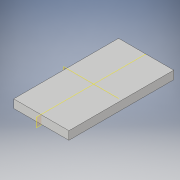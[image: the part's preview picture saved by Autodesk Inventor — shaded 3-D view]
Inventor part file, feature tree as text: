
AUTODESK INVENTOR PART (.ipt)
format: ipt  version: 2017 (Build 210142000, 142)  size: 172,032 bytes
history: native  units: in
note: dims shown in document units (in); Inventor stores cm internally (conversion verified against a paired STEP export)
features: extrude x4, sketch x4, plane x2, mirror x2, projected_geometry x1
ambient origin geometry x8: Origin, YZ Plane, XZ Plane, XY Plane, X Axis, Y Axis, Z Axis, Center Point
bodies: Solid1 (feature_tree)
feature tree (13):
  extrude  "Extrusion1"  Depth=76.0in
  extrude  "Extrusion2"  Depth=1.0in
  extrude  "Extrusion3"  Depth=2.0in TaperAngle=0.0deg
  plane  "Work Plane1"
  mirror  "Mirror1"
  extrude  "Extrusion4"  Depth=18.0in
  plane  "Work Plane2"
  mirror  "Mirror2"
  sketch  "Sketch1"  dims[d0=40.0in d1=76.0in]
  sketch  "Sketch2"  dims[d2=6.0in d3=0.0in d4=1.0in]
  sketch  "Sketch3"  dims[d5=1.0in d6=2.0in d7=0.0in]
  projected_geometry  "Projected Loop1"
  sketch  "Sketch4"  dims[d8=1.0in d9=18.0in d10=10.0in d11=1.0in d12=18.0in d13=10.0in d14=2.0in d15=0.0in d16=6.0in d17=1.0in d18=6.0in d19=1.0in d20=7.0in d21=7.0in d22=2.0in d23=0.0in]
